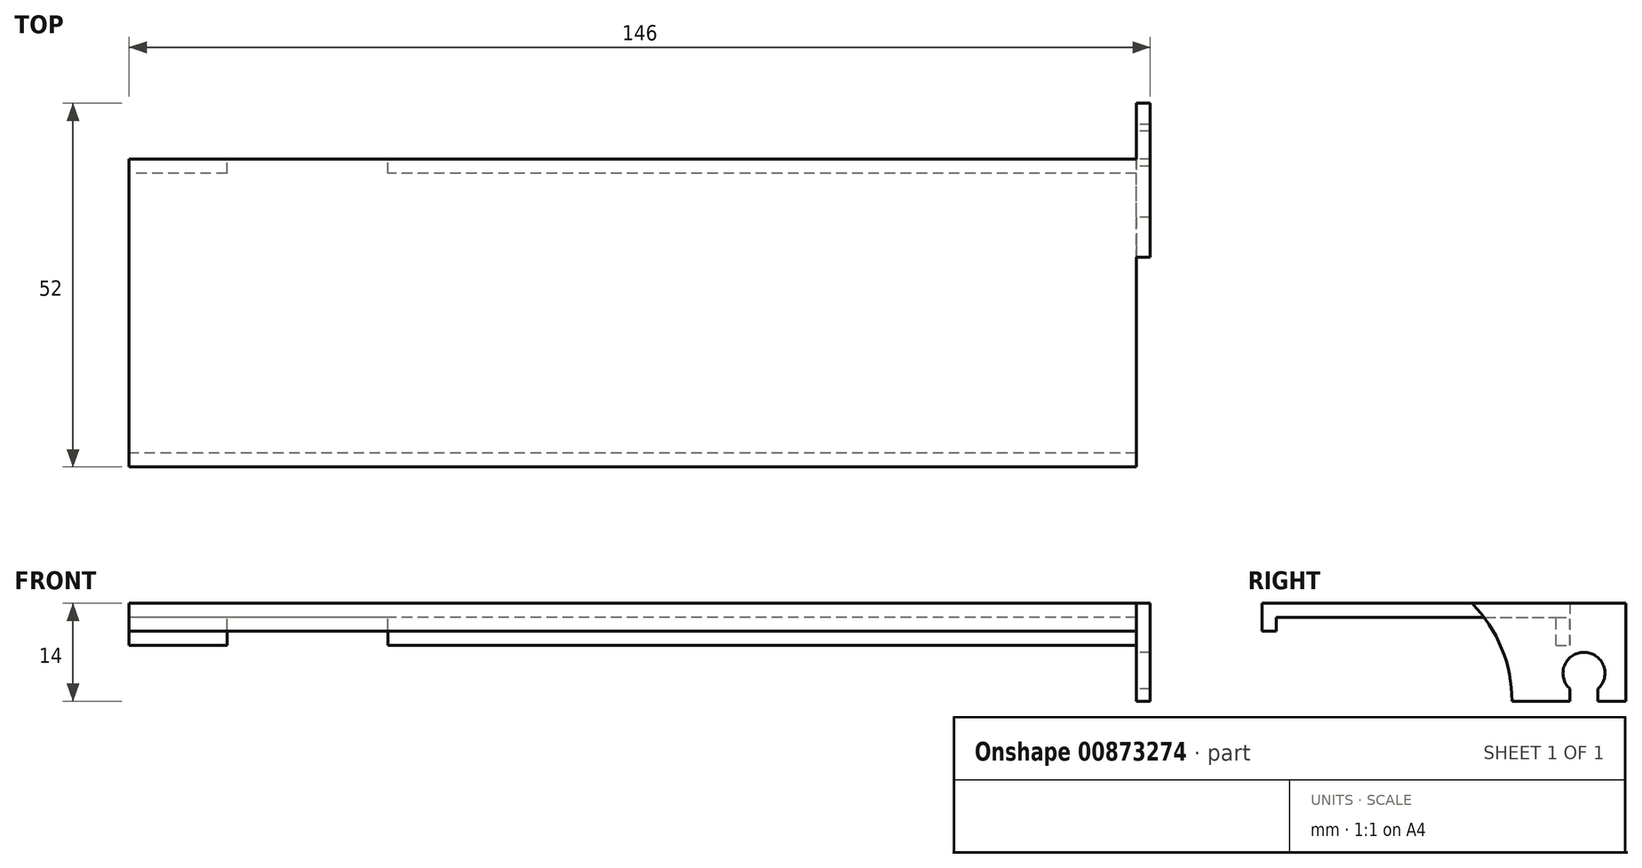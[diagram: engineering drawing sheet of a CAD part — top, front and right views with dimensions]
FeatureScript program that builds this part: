
annotation { "Feature Type Name" : "Feature", "Feature Type Description" : "" }
export const myFeature = defineFeature(function(context is Context, id is Id, definition is map)
    precondition{}
    {
        {
            var Q0;
            Q0=qCreatedBy(makeId("Right.planeOp"),FACE);
            var sketch = newSketch(context, id + "F0", { "sketchPlane" : qUnion([Q0])});
            skLineSegment(sketch, "E0", {"start": v(-20, 23) * mm, "end": v(-20, 25) * mm});
            skLineSegment(sketch, "E1", {"start": v(-20, 25) * mm, "end": v(20, 25) * mm});
            skLineSegment(sketch, "E2", {"start": v(20, 25) * mm, "end": v(20, 21) * mm});
            skLineSegment(sketch, "E3", {"start": v(0, 27.82) * mm, "end": v(0, 25) * mm, "construction": true});
            skLineSegment(sketch, "E4", {"start": v(-20, 23) * mm, "end": v(-22, 23) * mm});
            skLineSegment(sketch, "E5", {"start": v(-22, 23) * mm, "end": v(-22, 27) * mm});
            skLineSegment(sketch, "E6", {"start": v(-22, 27) * mm, "end": v(22, 27) * mm});
            skLineSegment(sketch, "E7", {"start": v(22, 27) * mm, "end": v(22, 21) * mm});
            skLineSegment(sketch, "E8", {"start": v(22, 21) * mm, "end": v(20, 21) * mm});
            skSolve(sketch);
        }
        {
            var Q0;
            Q0 = qSketchRegion(id + "F0", true);
            extrude(context, id + "F1", {"entities" : qUnion([Q0]), "endBound" : BoundingType.SYMMETRIC, "depth" : 144 * mm, "offsetDistance" : 25 * mm});
        }
        {
            var Q0;
            Q0=makeQuery(id+"F1.opExtrude","CAP_FACE",FACE,{"disambiguationData":[OSD([sQuery(id+"F0.wireOp",EDGE,"E0"),sQuery(id+"F0.wireOp",EDGE,"E1"),sQuery(id+"F0.wireOp",EDGE,"E2"),sQuery(id+"F0.wireOp",EDGE,"E4"),sQuery(id+"F0.wireOp",EDGE,"E5"),sQuery(id+"F0.wireOp",EDGE,"E6"),sQuery(id+"F0.wireOp",EDGE,"E7"),sQuery(id+"F0.wireOp",EDGE,"E8")])],"isStart":false});
            var sketch = newSketch(context, id + "F2", { "sketchPlane" : qUnion([Q0])});
            skLineSegment(sketch, "E9", {"start": v(22, 27) * mm, "end": v(8, 27) * mm});
            skArc(sketch, "E10", {"start": v(26, 14.76) * mm, "mid": v(24, 20) * mm, "end": v(22, 14.76) * mm});
            skLineSegment(sketch, "E11", {"start": v(13.72, 13) * mm, "end": v(22, 13) * mm});
            skLineSegment(sketch, "E12", {"start": v(30, 13) * mm, "end": v(30, 27) * mm});
            skLineSegment(sketch, "E13", {"start": v(30, 27) * mm, "end": v(22, 27) * mm});
            skArc(sketch, "E14", {"start": v(13.72, 13) * mm, "mid": v(12.23, 20.56) * mm, "end": v(8, 27) * mm});
            skLineSegment(sketch, "E15", {"start": v(22, 14.76) * mm, "end": v(22, 13) * mm});
            skLineSegment(sketch, "E16", {"start": v(26, 14.76) * mm, "end": v(26, 13) * mm});
            skLineSegment(sketch, "E17.trimOffspring", {"start": v(26, 13) * mm, "end": v(30, 13) * mm});
            skSolve(sketch);
        }
        {
            var Q0;
            Q0 = qSketchRegion(id + "F2", true);
            extrude(context, id + "F3", {"entities" : qUnion([Q0]), "operationType" : NewBodyOperationType.ADD, "depth" : 2 * mm, "offsetDistance" : 25 * mm});
        }
        {
            var Q0;
            Q0=makeQuery(id+"F1.opExtrude","SWEPT_FACE",FACE,{"disambiguationData":[OSD([sQuery(id+"F0.wireOp",EDGE,"E7")])]});
            var sketch = newSketch(context, id + "F4", { "sketchPlane" : qUnion([Q0])});
            skLineSegment(sketch, "E18.bottom", {"start": v(35, 21) * mm, "end": v(58, 21) * mm});
            skLineSegment(sketch, "E18.left", {"start": v(35, 21) * mm, "end": v(35, 25) * mm});
            skLineSegment(sketch, "E18.right", {"start": v(58, 21) * mm, "end": v(58, 25) * mm});
            skLineSegment(sketch, "E19", {"start": v(35, 25) * mm, "end": v(58, 25) * mm});
            skSolve(sketch);
        }
        {
            var Q0;
            Q0 = qSketchRegion(id + "F4", true);
            extrude(context, id + "F5", {"entities" : qUnion([Q0]), "operationType" : NewBodyOperationType.REMOVE, "oppositeDirection" : true, "depth" : 25 * mm, "offsetDistance" : 25 * mm});
        }
    });
